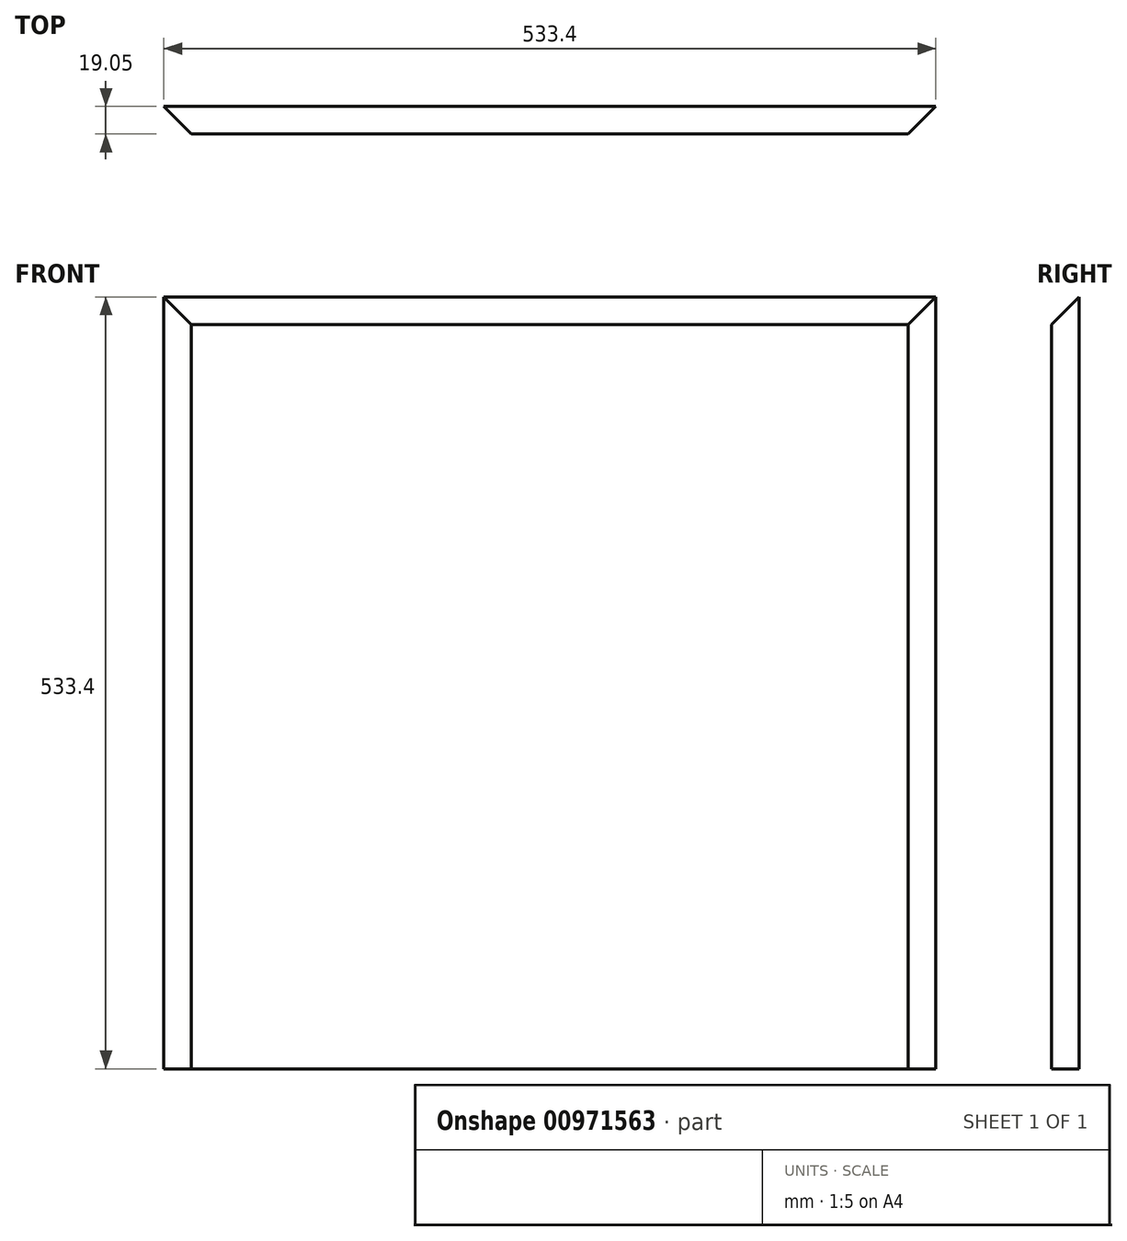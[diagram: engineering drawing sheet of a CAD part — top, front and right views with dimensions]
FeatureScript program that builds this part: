
annotation { "Feature Type Name" : "Feature", "Feature Type Description" : "" }
export const myFeature = defineFeature(function(context is Context, id is Id, definition is map)
    precondition{}
    {
        {
            var Q0;
            Q0=qCreatedBy(makeId("Front.planeOp"),FACE);
            var sketch = newSketch(context, id + "F0", { "sketchPlane" : qUnion([Q0])});
            skLineSegment(sketch, "E0.bottom", {"start": v(-265.05, 331.82) * mm, "end": v(268.35, 331.82) * mm});
            skLineSegment(sketch, "E0.top", {"start": v(-265.05, -201.58) * mm, "end": v(268.35, -201.58) * mm});
            skLineSegment(sketch, "E0.left", {"start": v(-265.05, 331.82) * mm, "end": v(-265.05, -201.58) * mm});
            skLineSegment(sketch, "E0.right", {"start": v(268.35, 331.82) * mm, "end": v(268.35, -201.58) * mm});
            skSolve(sketch);
        }
        {
            var Q0;
            Q0=makeQuery(id+"F0.imprint","IMPRINT",FACE,{"disambiguationData":[TD([[makeQuery(id+"F0.imprint","IMPRINT",EDGE,{"derivedFrom":sQuery(id+"F0.wireOp",EDGE,"E0.bottom")}),-1.0]])]});
            extrude(context, id + "F1", {"entities" : qUnion([Q0]), "depth" : 19.05 * mm, "offsetDistance" : 25.4 * mm});
        }
        {
            var Q0;
            Q0=makeQuery(id+"F1.opExtrude","CAP_EDGE",EDGE,{"disambiguationData":[OSD([sQuery(id+"F0.wireOp",EDGE,"E0.bottom")])],"isStart":false});
            var Q1;
            Q1=makeQuery(id+"F1.opExtrude","CAP_EDGE",EDGE,{"disambiguationData":[OSD([sQuery(id+"F0.wireOp",EDGE,"E0.left")])],"isStart":false});
            var Q2;
            Q2=makeQuery(id+"F1.opExtrude","CAP_EDGE",EDGE,{"disambiguationData":[OSD([sQuery(id+"F0.wireOp",EDGE,"E0.right")])],"isStart":false});
            chamfer(context, id + "F2", {"entities" : qUnion([Q0, Q1, Q2]), "width" : 19.05 * mm});
        }
    });
